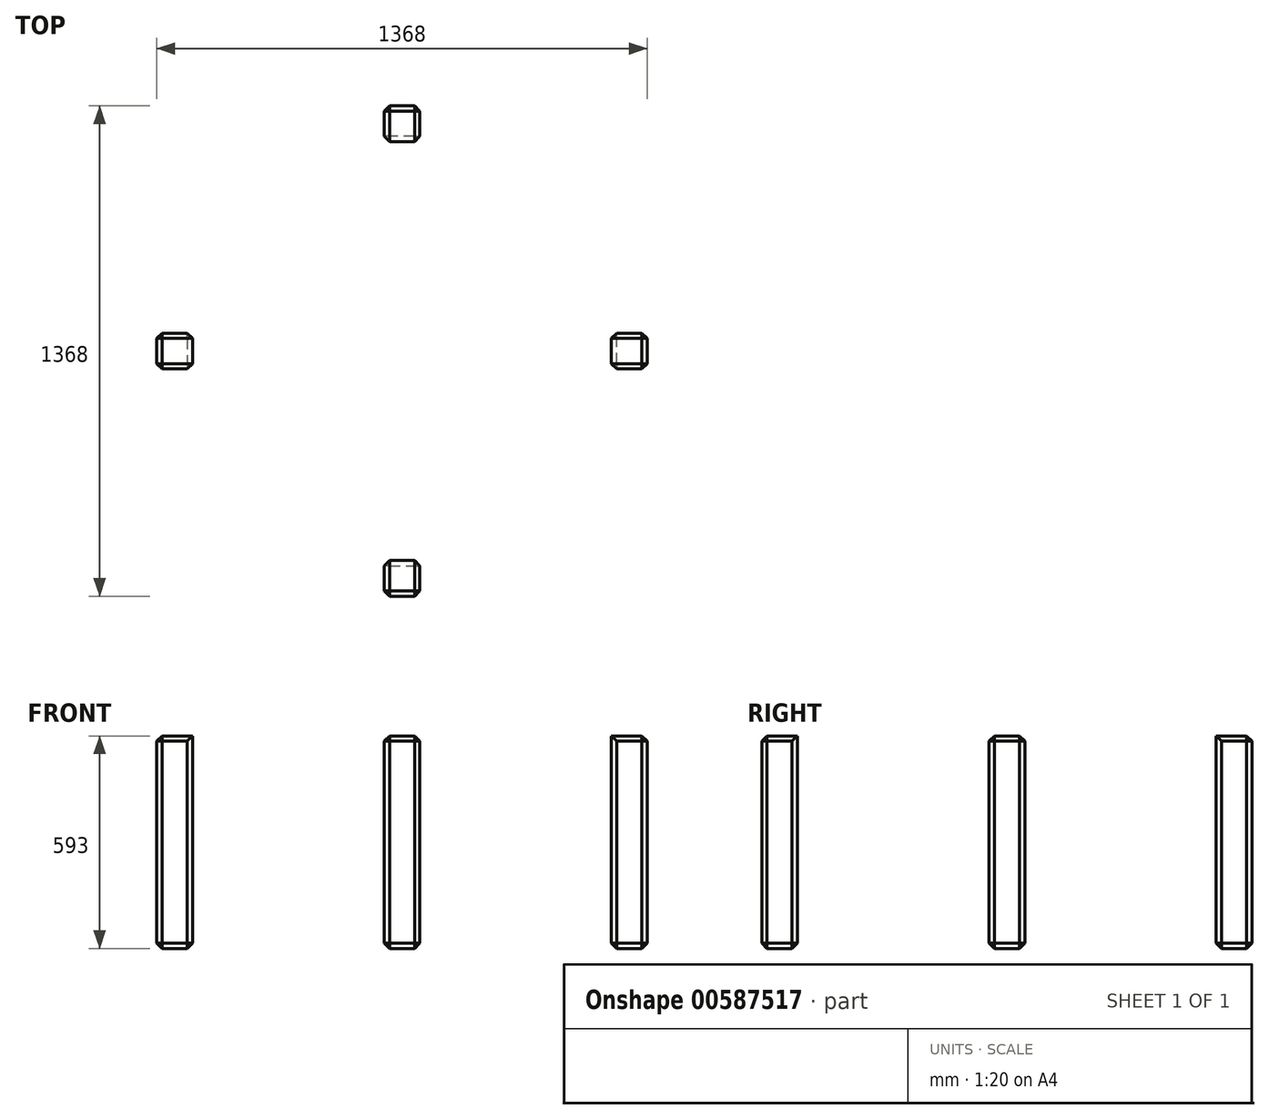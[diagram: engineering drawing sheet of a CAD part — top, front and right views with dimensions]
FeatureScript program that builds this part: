
annotation { "Feature Type Name" : "Feature", "Feature Type Description" : "" }
export const myFeature = defineFeature(function(context is Context, id is Id, definition is map)
    precondition{}
    {
        {
            var Q0;
            Q0=qCreatedBy(makeId("Front.planeOp"),FACE);
            var sketch = newSketch(context, id + "F0", { "sketchPlane" : qUnion([Q0])});
            skLineSegment(sketch, "E0", {"start": v(0, 0) * mm, "end": v(0, 1798.37) * mm, "construction": true});
            skLineSegment(sketch, "E1", {"start": v(0, 1798.37) * mm, "end": v(0, 100.3) * mm, "construction": true});
            skLineSegment(sketch, "E2", {"start": v(634, 567.28) * mm, "end": v(634, 1543.65) * mm});
            skLineSegment(sketch, "E3", {"start": v(619.18, 1562.97) * mm, "end": v(200, 1675.29) * mm});
            skLineSegment(sketch, "E4", {"start": v(200, 1675.29) * mm, "end": v(0, 1675.29) * mm});
            skLineSegment(sketch, "E5", {"start": v(628.14, 553.14) * mm, "end": v(75, 0) * mm});
            skLineSegment(sketch, "E6", {"start": v(75, 0) * mm, "end": v(0, 0) * mm});
            skPoint(sketch, "E7.visualSharp", {"position": v(634, 1559) * mm});
            skArc(sketch, "E7.filletArc", {"start": v(634, 1543.65) * mm, "mid": v(629.87, 1555.83) * mm, "end": v(619.18, 1562.97) * mm});
            skPoint(sketch, "E8.visualSharp", {"position": v(634, 559) * mm});
            skArc(sketch, "E8.filletArc", {"start": v(628.14, 553.14) * mm, "mid": v(632.48, 559.63) * mm, "end": v(634, 567.28) * mm});
            skSolve(sketch);
        }
        {
            var Q0;
            Q0=sQuery(id+"F0.wireOp",EDGE,"E4");
            var Q1;
            Q1=sQuery(id+"F0.wireOp",EDGE,"E3");
            var Q2;
            Q2=sQuery(id+"F0.wireOp",EDGE,"E7.filletArc");
            var Q3;
            Q3=sQuery(id+"F0.wireOp",EDGE,"E2");
            var Q4;
            Q4=sQuery(id+"F0.wireOp",EDGE,"E5");
            var Q5;
            Q5=sQuery(id+"F0.wireOp",EDGE,"E6");
            var Q6;
            Q6=sQuery(id+"F0.wireOp",EDGE,"E8.filletArc");
            var Q7;
            Q7=sQuery(id+"F0.wireOp",EDGE,"E1");
            revolve(context, id + "F1", {"bodyType" : ExtendedToolBodyType.SURFACE, "surfaceEntities" : qUnion([Q0, Q1, Q2, Q3, Q4, Q5, Q6]), "axis" : qUnion([Q7]), "revolveType" : RevolveType.FULL});
        }
        {
            var Q0;
            Q0=qCreatedBy(makeId("Top.planeOp"),FACE);
            cPlane(context, id + "F2", {"entities" : qUnion([Q0]), "cplaneType" : CPlaneType.OFFSET, "offset" : 550 * mm, "width" : 150 * mm, "height" : 150 * mm});
        }
        {
            var Q0;
            Q0=qCreatedBy(id+"F2.planeOp",FACE);
            var sketch = newSketch(context, id + "F3", { "sketchPlane" : qUnion([Q0])});
            skLineSegment(sketch, "E9", {"start": v(0, 668.6) * mm, "end": v(0, -732.78) * mm, "construction": true});
            skLineSegment(sketch, "E10", {"start": v(-729.39, 0) * mm, "end": v(801.13, 0) * mm, "construction": true});
            skLineSegment(sketch, "E11.bottom", {"start": v(-50, -584) * mm, "end": v(50, -584) * mm});
            skLineSegment(sketch, "E11.top", {"start": v(-50, -684) * mm, "end": v(50, -684) * mm});
            skLineSegment(sketch, "E11.left", {"start": v(-50, -584) * mm, "end": v(-50, -684) * mm});
            skLineSegment(sketch, "E11.right", {"start": v(50, -584) * mm, "end": v(50, -684) * mm});
            skLineSegment(sketch, "E12", {"start": v(-50, -634) * mm, "end": v(50, -634) * mm, "construction": true});
            skPoint(sketch, "E13", {"position": v(0, -634) * mm});
            skArc(sketch, "E14.trimOffspring", {"start": v(-50, -632.03) * mm, "mid": v(0, -634) * mm, "end": v(50, -632.03) * mm});
            skSolve(sketch);
        }
        {
            var Q0;
            Q0 = qSketchRegion(id + "F3", true);
            extrude(context, id + "F4", {"entities" : qUnion([Q0]), "oppositeDirection" : true, "depth" : 500 * mm, "offsetDistance" : 25 * mm, "hasSecondDirection" : true, "secondDirectionOppositeDirection" : false, "secondDirectionDepth" : 93 * mm});
        }
        {
            var Q0;
            Q0=makeQuery(id+"F4.opExtrude","SWEPT_EDGE",EDGE,{"disambiguationData":[OSD([sQuery(id+"F3.wireOp",EDGE,"E11.top"),sQuery(id+"F3.wireOp",EDGE,"E11.right")])]});
            var Q1;
            Q1=makeQuery(id+"F4.opExtrude","CAP_EDGE",EDGE,{"disambiguationData":[OSD([sQuery(id+"F3.wireOp",EDGE,"E11.right")])],"isStart":true});
            var Q2;
            Q2=makeQuery(id+"F4.opExtrude","CAP_EDGE",EDGE,{"disambiguationData":[OSD([sQuery(id+"F3.wireOp",EDGE,"E11.top")])],"isStart":true});
            var Q3;
            Q3=makeQuery(id+"F4.opExtrude","CAP_EDGE",EDGE,{"disambiguationData":[OSD([sQuery(id+"F3.wireOp",EDGE,"E11.left")])],"isStart":true});
            var Q4;
            Q4=makeQuery(id+"F4.opExtrude","SWEPT_EDGE",EDGE,{"disambiguationData":[OSD([sQuery(id+"F3.wireOp",EDGE,"E11.bottom"),sQuery(id+"F3.wireOp",EDGE,"E11.right")])]});
            var Q5;
            Q5=makeQuery(id+"F4.opExtrude","SWEPT_EDGE",EDGE,{"disambiguationData":[OSD([sQuery(id+"F3.wireOp",EDGE,"E11.bottom"),sQuery(id+"F3.wireOp",EDGE,"E11.left")])]});
            var Q6;
            Q6=makeQuery(id+"F4.opExtrude","SWEPT_EDGE",EDGE,{"disambiguationData":[OSD([sQuery(id+"F3.wireOp",EDGE,"E11.top"),sQuery(id+"F3.wireOp",EDGE,"E11.left")])]});
            var Q7;
            Q7=makeQuery(id+"F4.opExtrude","CAP_EDGE",EDGE,{"disambiguationData":[OSD([sQuery(id+"F3.wireOp",EDGE,"E11.top")])],"isStart":false});
            var Q8;
            Q8=makeQuery(id+"F4.opExtrude","CAP_EDGE",EDGE,{"disambiguationData":[OSD([sQuery(id+"F3.wireOp",EDGE,"E11.left")])],"isStart":false});
            var Q9;
            Q9=makeQuery(id+"F4.opExtrude","CAP_EDGE",EDGE,{"disambiguationData":[OSD([sQuery(id+"F3.wireOp",EDGE,"E11.bottom")])],"isStart":false});
            var Q10;
            Q10=makeQuery(id+"F4.opExtrude","CAP_EDGE",EDGE,{"disambiguationData":[OSD([sQuery(id+"F3.wireOp",EDGE,"E11.right")])],"isStart":false});
            chamfer(context, id + "F5", {"entities" : qUnion([Q0, Q1, Q2, Q3, Q4, Q5, Q6, Q7, Q8, Q9, Q10]), "width" : 15 * mm, "tangentPropagation" : true});
        }
        {
            var Q0;
            Q0=makeQuery(id+"F4.opExtrude","SWEPT_BODY",BODY,{"disambiguationData":[OSD([sQuery(id+"F3.wireOp",EDGE,"E11.bottom"),sQuery(id+"F3.wireOp",EDGE,"E11.top"),sQuery(id+"F3.wireOp",EDGE,"E11.left"),sQuery(id+"F3.wireOp",EDGE,"E11.right")])]});
            var Q1;
            Q1=makeQuery(id+"F1.opRevolve","SWEPT_FACE",FACE,{"disambiguationData":[OSD([sQuery(id+"F0.wireOp",EDGE,"E2")])]});
            circularPattern(context, id + "F6", {"entities" : qUnion([Q0]), "axis" : qUnion([Q1]), "angle" : 360 * degree, "instanceCount" : 4, "equalSpace" : true});
        }
    });
